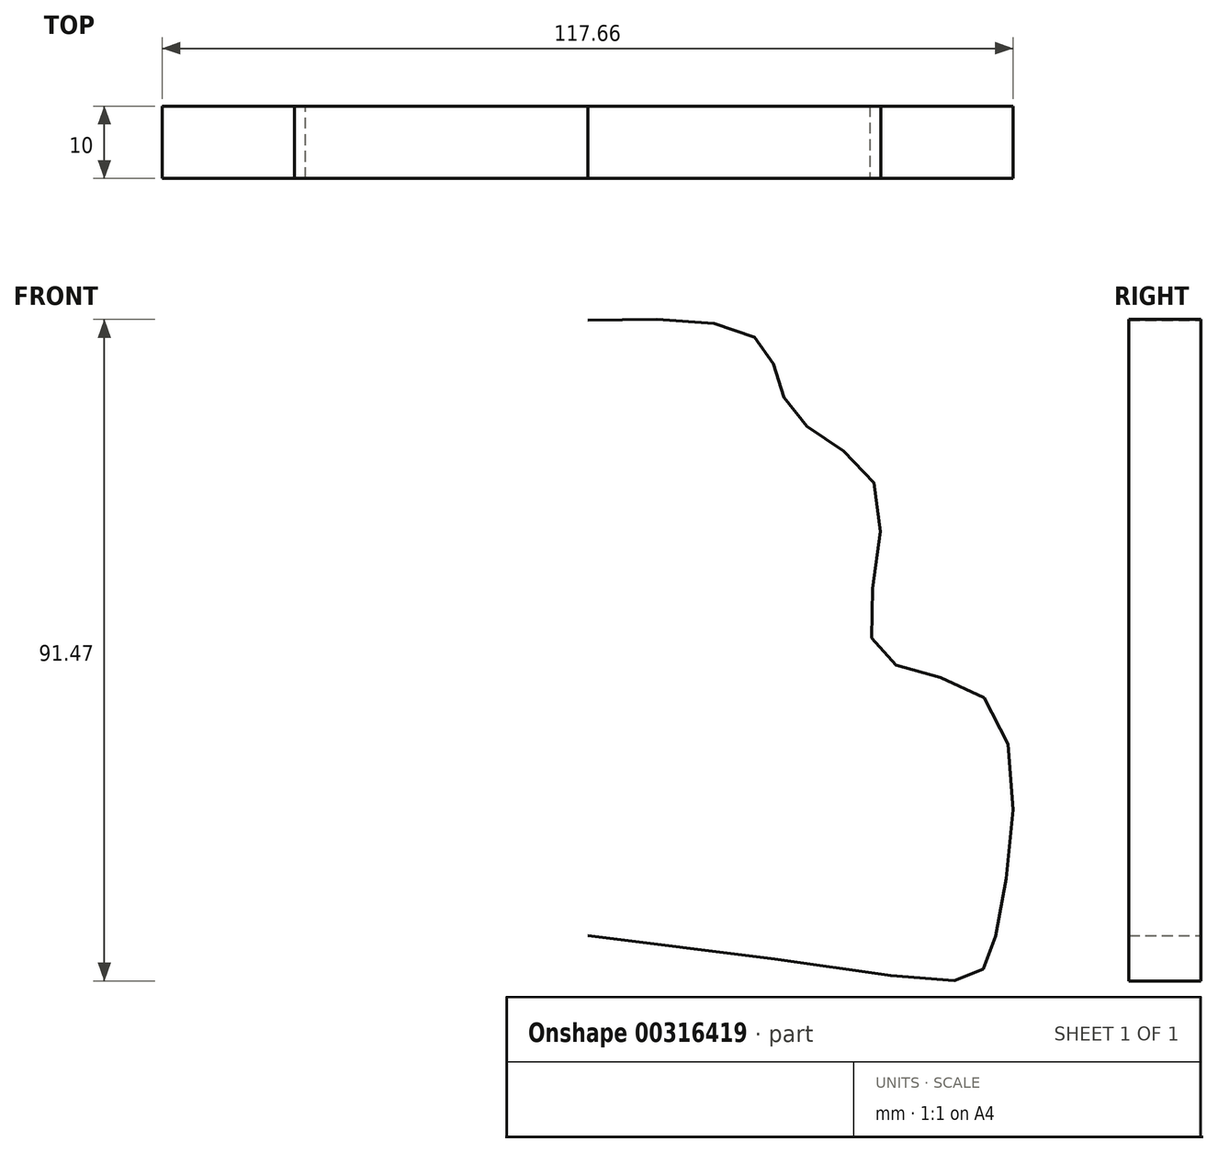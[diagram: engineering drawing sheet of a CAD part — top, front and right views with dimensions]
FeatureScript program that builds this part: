
annotation { "Feature Type Name" : "Feature", "Feature Type Description" : "" }
export const myFeature = defineFeature(function(context is Context, id is Id, definition is map)
    precondition{}
    {
        {
            var Q0;
            Q0=qCreatedBy(makeId("Front.planeOp"),FACE);
            var sketch = newSketch(context, id + "F0", { "sketchPlane" : qUnion([Q0])});
            skFitSpline(sketch, "E0", {"points": [v(0, 61.35) * mm, v(-24.26, 58.02) * mm, v(-28.35, 48.52) * mm, v(-39.99, 37.9) * mm, v(-39.97, 15.72) * mm, v(-55.4, 8.56) * mm, v(-56.52, -23.33) * mm, v(0, -23.74) * mm], "startDerivative": vector(-233.48, 6.33) * mm, "endDerivative": vector(726.1, 79.2) * mm});
            skFitSpline(sketch, "E1.MirrorCS", {"points": [v(0, 61.35) * mm, v(24.26, 58.02) * mm, v(28.35, 48.52) * mm, v(39.99, 37.9) * mm, v(39.97, 15.72) * mm, v(55.4, 8.56) * mm, v(56.52, -23.33) * mm, v(0, -23.74) * mm], "startDerivative": vector(233.48, 6.33) * mm, "endDerivative": vector(-726.1, 79.2) * mm});
            skSolve(sketch);
        }
        {
            var Q0;
            Q0 = qSketchRegion(id + "F0", true);
            extrude(context, id + "F1", {"entities" : qUnion([Q0]), "depth" : 10 * mm});
        }
    });
